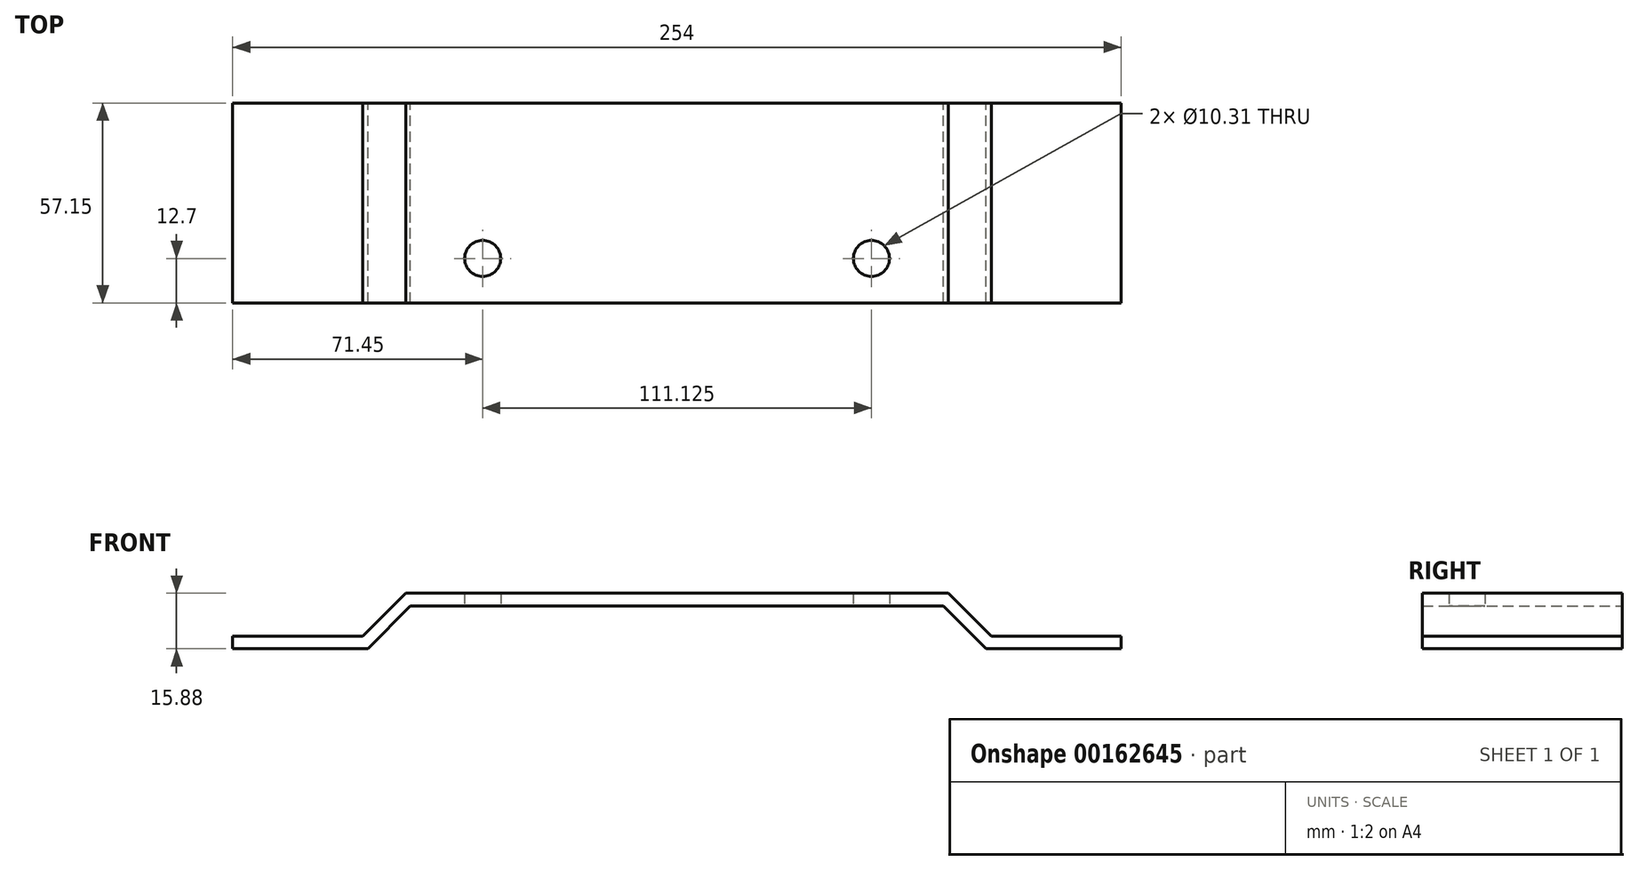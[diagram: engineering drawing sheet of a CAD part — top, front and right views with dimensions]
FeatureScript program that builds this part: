
annotation { "Feature Type Name" : "Feature", "Feature Type Description" : "" }
export const myFeature = defineFeature(function(context is Context, id is Id, definition is map)
    precondition{}
    {
        {
            var Q0;
            Q0=qCreatedBy(makeId("Front.planeOp"),FACE);
            var sketch = newSketch(context, id + "F0", { "sketchPlane" : qUnion([Q0])});
            skLineSegment(sketch, "E0.bottom", {"start": v(0, 0) * mm, "end": v(38.63, 0) * mm});
            skLineSegment(sketch, "E0.left", {"start": v(0, 0) * mm, "end": v(0, 3.57) * mm});
            skLineSegment(sketch, "E0.right", {"start": v(254, 0) * mm, "end": v(254, 3.57) * mm});
            skLineSegment(sketch, "E1.0", {"start": v(0, 3.57) * mm, "end": v(37.15, 3.57) * mm});
            skLineSegment(sketch, "E2", {"start": v(127, 12.17) * mm, "end": v(127, 0) * mm});
            skLineSegment(sketch, "E3", {"start": v(51.97, 12.17) * mm, "end": v(51.97, 0) * mm});
            skLineSegment(sketch, "E4", {"start": v(50.8, 12.17) * mm, "end": v(50.8, 0) * mm});
            skLineSegment(sketch, "E5", {"start": v(50.8, 12.17) * mm, "end": v(38.63, 0) * mm});
            skLineSegment(sketch, "E6.0", {"start": v(49.45, 15.88) * mm, "end": v(37.15, 3.57) * mm});
            skLineSegment(sketch, "E7.MirrorCS", {"start": v(203.2, 12.17) * mm, "end": v(215.37, 0) * mm});
            skLineSegment(sketch, "E8.MirrorCS", {"start": v(204.55, 15.88) * mm, "end": v(216.85, 3.57) * mm});
            skLineSegment(sketch, "E9.trimOffspring", {"start": v(50.8, 12.17) * mm, "end": v(203.2, 12.17) * mm});
            skLineSegment(sketch, "E10.trimOffspring", {"start": v(49.45, 15.88) * mm, "end": v(204.55, 15.88) * mm});
            skLineSegment(sketch, "E11.trimOffspring", {"start": v(216.85, 3.57) * mm, "end": v(254, 3.57) * mm});
            skLineSegment(sketch, "E12.trimOffspring", {"start": v(215.37, 0) * mm, "end": v(254, 0) * mm});
            skLineSegment(sketch, "E13.trimOffspring", {"start": v(50.8, 0) * mm, "end": v(51.97, 0) * mm});
            skPoint(sketch, "E14.orphan", {"position": v(51.97, 15.88) * mm});
            skPoint(sketch, "E15.orphan", {"position": v(127, 15.88) * mm});
            skPoint(sketch, "E0.top.end.orphan", {"position": v(35.28, 15.88) * mm});
            skPoint(sketch, "E16.orphan", {"position": v(0, 15.88) * mm});
            skSolve(sketch);
        }
        {
            var Q0;
            Q0=makeQuery(id+"F0.imprint","IMPRINT",FACE,{"disambiguationData":[TD([[makeQuery(id+"F0.imprint","IMPRINT",EDGE,{"derivedFrom":sQuery(id+"F0.wireOp",EDGE,"E0.bottom")}),1.0]])]});
            extrude(context, id + "F1", {"entities" : qUnion([Q0]), "depth" : 57.15 * mm});
        }
        {
            var Q0;
            Q0=makeQuery(id+"F1.opExtrude","SWEPT_FACE",FACE,{"disambiguationData":[OSD([sQuery(id+"F0.wireOp",EDGE,"E0.bottom")])]});
            var sketch = newSketch(context, id + "F2", { "sketchPlane" : qUnion([Q0])});
            skCircle(sketch, "E17", {"center": v(71.45, 44.45) * mm, "radius": 5.16 * mm});
            skCircle(sketch, "E18", {"center": v(182.58, 44.45) * mm, "radius": 5.16 * mm});
            skSolve(sketch);
        }
        {
            var Q0;
            Q0=makeQuery(id+"F2.imprint","IMPRINT",FACE,{"disambiguationData":[TD([[makeQuery(id+"F2.imprint","IMPRINT",EDGE,{"derivedFrom":sQuery(id+"F2.wireOp",EDGE,"E17")}),1.0]])]});
            var Q1;
            Q1=makeQuery(id+"F2.imprint","IMPRINT",FACE,{"disambiguationData":[TD([[makeQuery(id+"F2.imprint","IMPRINT",EDGE,{"derivedFrom":sQuery(id+"F2.wireOp",EDGE,"E18")}),1.0]])]});
            extrude(context, id + "F3", {"entities" : qUnion([Q0, Q1]), "operationType" : NewBodyOperationType.REMOVE, "oppositeDirection" : true, "depth" : 25.4 * mm});
        }
    });
